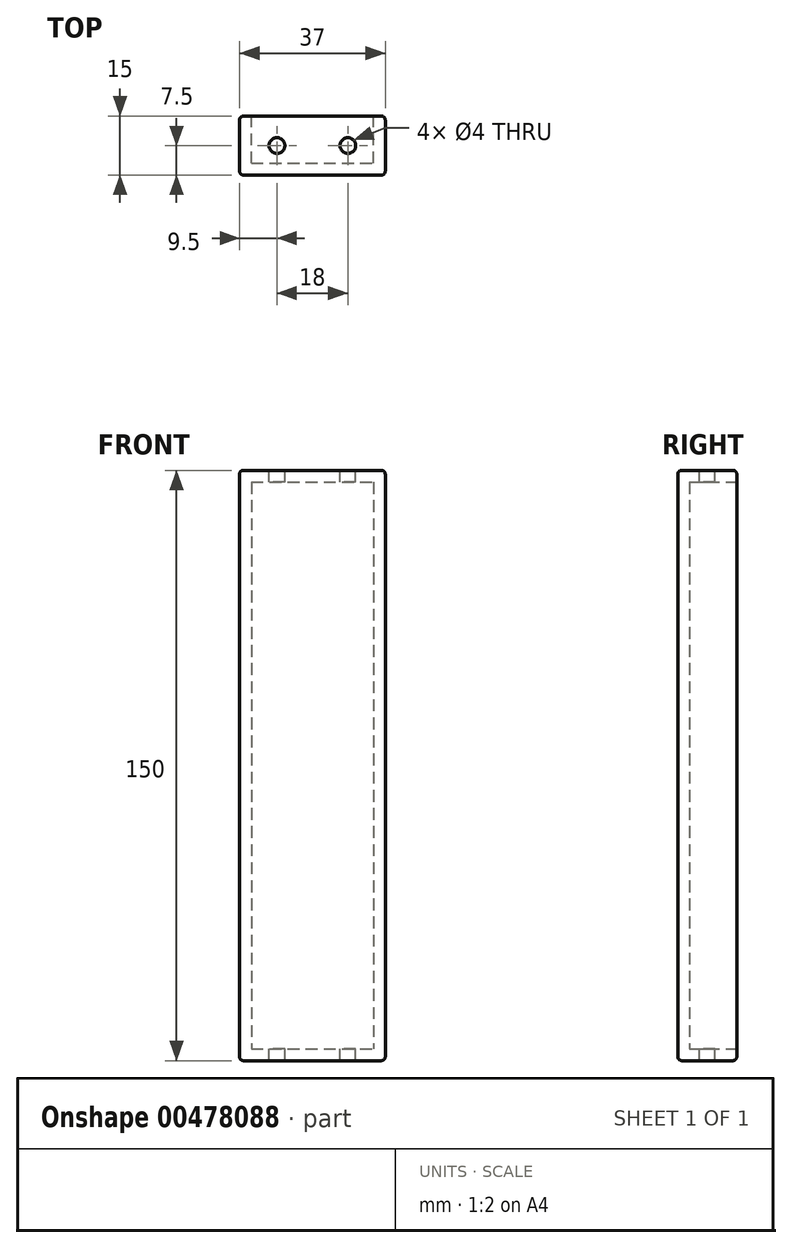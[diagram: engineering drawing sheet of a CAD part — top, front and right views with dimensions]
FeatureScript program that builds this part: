
annotation { "Feature Type Name" : "Feature", "Feature Type Description" : "" }
export const myFeature = defineFeature(function(context is Context, id is Id, definition is map)
    precondition{}
    {
        {
            var Q0;
            Q0=qCreatedBy(makeId("Top.planeOp"),FACE);
            var sketch = newSketch(context, id + "F0", { "sketchPlane" : qUnion([Q0])});
            skLineSegment(sketch, "E0", {"start": v(-25.48, 0) * mm, "end": v(28.63, 0) * mm, "construction": true});
            skLineSegment(sketch, "E1", {"start": v(0, 28.13) * mm, "end": v(0, -28) * mm, "construction": true});
            skLineSegment(sketch, "E2.bottom", {"start": v(-18.5, 7.5) * mm, "end": v(18.5, 7.5) * mm});
            skLineSegment(sketch, "E2.top", {"start": v(-18.5, -7.5) * mm, "end": v(18.5, -7.5) * mm});
            skLineSegment(sketch, "E2.left", {"start": v(-18.5, 7.5) * mm, "end": v(-18.5, -7.5) * mm});
            skLineSegment(sketch, "E2.right", {"start": v(18.5, 7.5) * mm, "end": v(18.5, -7.5) * mm});
            skSolve(sketch);
        }
        {
            var Q0;
            Q0 = qSketchRegion(id + "F0", true);
            extrude(context, id + "F1", {"entities" : qUnion([Q0]), "depth" : 150 * mm});
        }
        {
            var Q0;
            Q0=makeQuery(id+"F1.opExtrude","SWEPT_FACE",FACE,{"disambiguationData":[OSD([sQuery(id+"F0.wireOp",EDGE,"E2.bottom")])]});
            var sketch = newSketch(context, id + "F2", { "sketchPlane" : qUnion([Q0])});
            skLineSegment(sketch, "E3.0", {"start": v(-15.5, 147) * mm, "end": v(-15.5, 3) * mm});
            skLineSegment(sketch, "E3.1", {"start": v(15.5, 147) * mm, "end": v(-15.5, 147) * mm});
            skLineSegment(sketch, "E3.2", {"start": v(15.5, 147) * mm, "end": v(15.5, 3) * mm});
            skLineSegment(sketch, "E3.3", {"start": v(15.5, 3) * mm, "end": v(-15.5, 3) * mm});
            skSolve(sketch);
        }
        {
            var Q0;
            Q0 = qSketchRegion(id + "F2", true);
            extrude(context, id + "F3", {"entities" : qUnion([Q0]), "operationType" : NewBodyOperationType.REMOVE, "oppositeDirection" : true, "depth" : 12 * mm});
        }
        {
            var Q0;
            Q0=makeQuery(id+"F1.opExtrude","CAP_FACE",FACE,{"disambiguationData":[OSD([sQuery(id+"F0.wireOp",EDGE,"E2.bottom"),sQuery(id+"F0.wireOp",EDGE,"E2.top"),sQuery(id+"F0.wireOp",EDGE,"E2.left"),sQuery(id+"F0.wireOp",EDGE,"E2.right")])],"isStart":false});
            var sketch = newSketch(context, id + "F4", { "sketchPlane" : qUnion([Q0])});
            skLineSegment(sketch, "E4", {"start": v(18.5, 0) * mm, "end": v(-18.5, 0) * mm, "construction": true});
            skLineSegment(sketch, "E5", {"start": v(0, -7.5) * mm, "end": v(0, 7.5) * mm, "construction": true});
            skCircle(sketch, "E6", {"center": v(9, 0) * mm, "radius": 2 * mm});
            skCircle(sketch, "E7", {"center": v(-9, 0) * mm, "radius": 2 * mm});
            skSolve(sketch);
        }
        {
            var Q0;
            Q0 = qSketchRegion(id + "F4", true);
            extrude(context, id + "F5", {"entities" : qUnion([Q0]), "operationType" : NewBodyOperationType.REMOVE, "endBound" : BoundingType.THROUGH_ALL, "oppositeDirection" : true, "depth" : 25 * mm});
        }
        {
            var Q0;
            Q0=makeQuery(id+"F1.opExtrude","CAP_EDGE",EDGE,{"disambiguationData":[OSD([sQuery(id+"F0.wireOp",EDGE,"E2.left")])],"isStart":false});
            var Q1;
            Q1=makeQuery(id+"F1.opExtrude","CAP_EDGE",EDGE,{"disambiguationData":[OSD([sQuery(id+"F0.wireOp",EDGE,"E2.right")])],"isStart":false});
            var Q2;
            Q2=makeQuery(id+"F1.opExtrude","CAP_EDGE",EDGE,{"disambiguationData":[OSD([sQuery(id+"F0.wireOp",EDGE,"E2.left")])],"isStart":true});
            var Q3;
            Q3=makeQuery(id+"F1.opExtrude","CAP_EDGE",EDGE,{"disambiguationData":[OSD([sQuery(id+"F0.wireOp",EDGE,"E2.right")])],"isStart":true});
            fillet(context, id + "F6", {"entities" : qUnion([Q0, Q1, Q2, Q3]), "radius" : 1 * mm, "tangentPropagation" : true, "allowEdgeOverflow" : false});
        }
        {
            var Q0;
            Q0=makeQuery(id+"F1.opExtrude","SWEPT_EDGE",EDGE,{"disambiguationData":[OSD([sQuery(id+"F0.wireOp",EDGE,"E2.top"),sQuery(id+"F0.wireOp",EDGE,"E2.right")])]});
            var Q1;
            Q1=makeQuery(id+"F1.opExtrude","SWEPT_EDGE",EDGE,{"disambiguationData":[OSD([sQuery(id+"F0.wireOp",EDGE,"E2.bottom"),sQuery(id+"F0.wireOp",EDGE,"E2.right")])]});
            fillet(context, id + "F7", {"entities" : qUnion([Q0, Q1]), "radius" : 1 * mm, "tangentPropagation" : true, "allowEdgeOverflow" : false});
        }
    });
